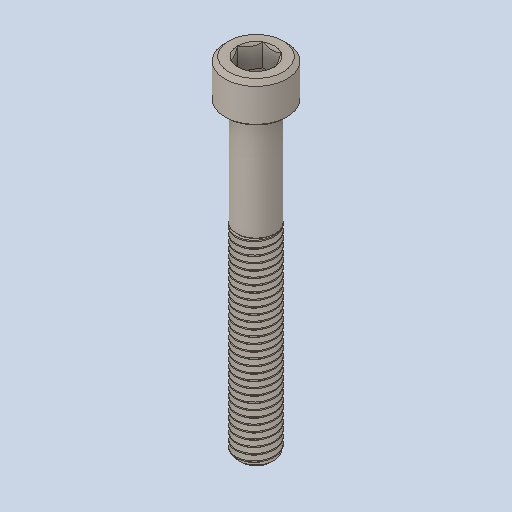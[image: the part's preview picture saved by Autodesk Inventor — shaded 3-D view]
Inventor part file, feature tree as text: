
AUTODESK INVENTOR PART (.ipt)
format: ipt  version: 2023.4 (Build 274418000, 418)  size: 683,008 bytes
history: native  units: in
note: dims shown in document units (in); Inventor stores cm internally (conversion verified against a paired STEP export)
features: fillet x1
ambient origin geometry x8: Origin, YZ Plane, XZ Plane, XY Plane, X Axis, Y Axis, Z Axis, Center Point
bodies: Solid1 (feature_tree)
feature tree (1):
  fillet  "Fillet1"  [1 undecoded]
note: 1 required parameter value undecoded (feature->parameter linkage not recoverable at this tier; creation-order binding heuristic only, values carry confidence <= 0.55)
